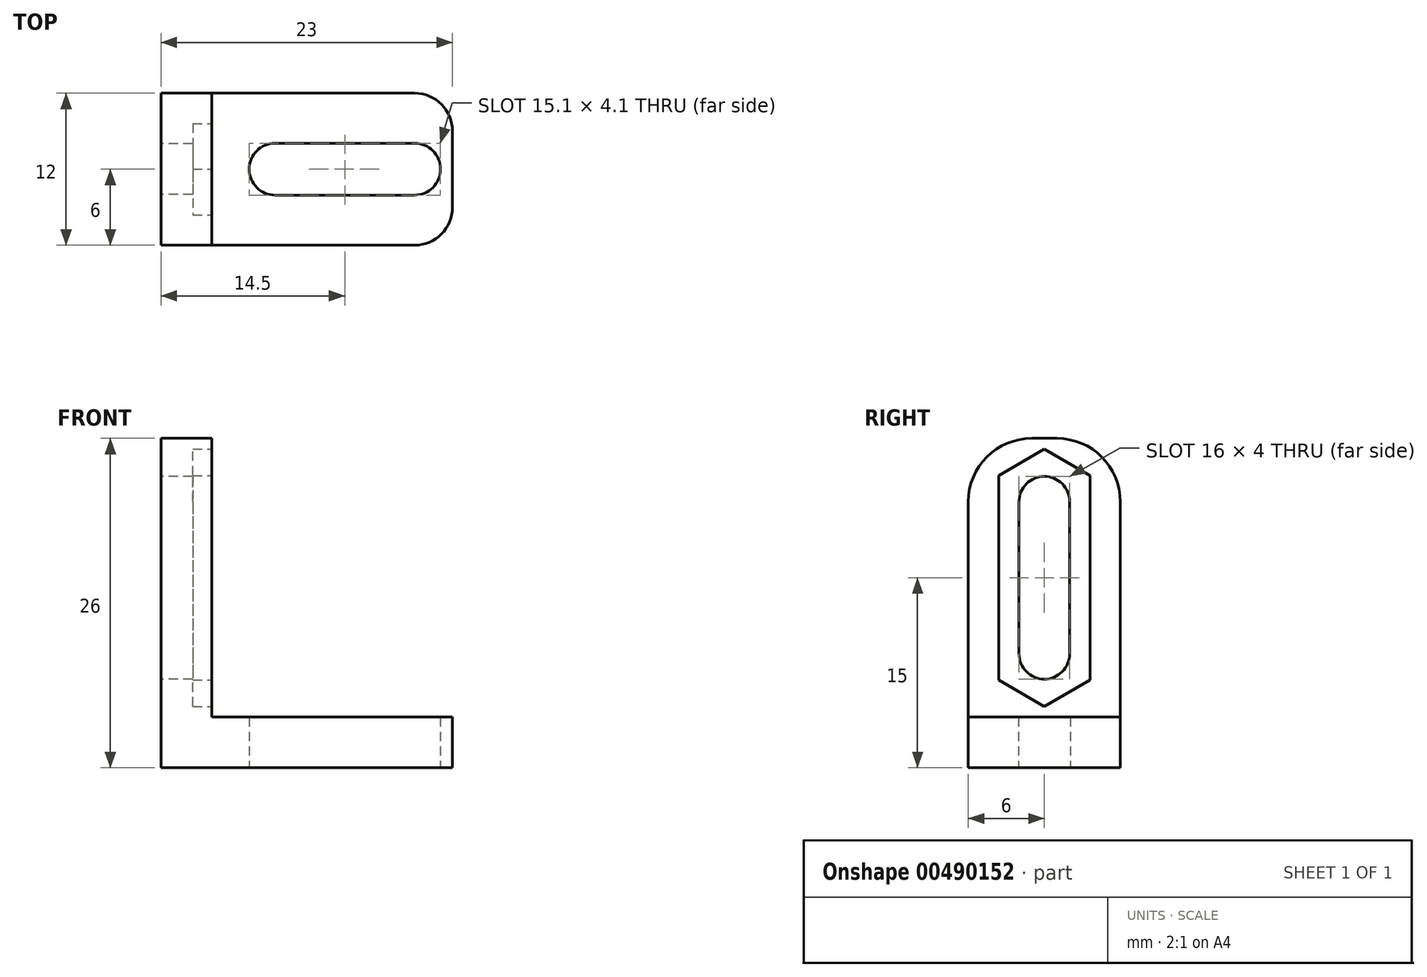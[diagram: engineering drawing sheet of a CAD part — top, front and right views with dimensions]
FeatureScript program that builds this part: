
annotation { "Feature Type Name" : "Feature", "Feature Type Description" : "" }
export const myFeature = defineFeature(function(context is Context, id is Id, definition is map)
    precondition{}
    {
        {
            var Q0;
            Q0=qCreatedBy(makeId("Top.planeOp"),FACE);
            var sketch = newSketch(context, id + "F0", { "sketchPlane" : qUnion([Q0])});
            skLineSegment(sketch, "E0.bottom", {"start": v(-3, 0) * mm, "end": v(-23, 0) * mm});
            skLineSegment(sketch, "E0.top", {"start": v(-3, -12) * mm, "end": v(-23, -12) * mm});
            skLineSegment(sketch, "E0.left", {"start": v(0, -3) * mm, "end": v(0, -9) * mm});
            skLineSegment(sketch, "E0.right", {"start": v(-23, 0) * mm, "end": v(-23, -12) * mm});
            skArc(sketch, "E1", {"start": v(-3, -8.05) * mm, "mid": v(-0.95, -6) * mm, "end": v(-3, -3.95) * mm});
            skPoint(sketch, "E1.centerSnap0", {"position": v(0, -6) * mm});
            skPoint(sketch, "E2.visualSharp", {"position": v(0, 0) * mm});
            skArc(sketch, "E2.filletArc", {"start": v(0, -3) * mm, "mid": v(-0.88, -0.88) * mm, "end": v(-3, 0) * mm});
            skPoint(sketch, "E3.visualSharp", {"position": v(0, -12) * mm});
            skArc(sketch, "E3.filletArc", {"start": v(-3, -12) * mm, "mid": v(-0.88, -11.12) * mm, "end": v(0, -9) * mm});
            skArc(sketch, "E4", {"start": v(-14, -3.95) * mm, "mid": v(-16.05, -6) * mm, "end": v(-14, -8.05) * mm});
            skLineSegment(sketch, "E5", {"start": v(-14, -3.95) * mm, "end": v(-3, -3.95) * mm});
            skLineSegment(sketch, "E6", {"start": v(-14, -8.05) * mm, "end": v(-3, -8.05) * mm});
            skSolve(sketch);
        }
        {
            var Q0;
            Q0=makeQuery(id+"F0.imprint","IMPRINT",FACE,{"disambiguationData":[TD([[makeQuery(id+"F0.imprint","IMPRINT",EDGE,{"derivedFrom":sQuery(id+"F0.wireOp",EDGE,"E0.bottom")}),1.0]])]});
            extrude(context, id + "F1", {"entities" : qUnion([Q0]), "depth" : 4 * mm, "offsetDistance" : 25 * mm});
        }
        {
            var Q0;
            Q0=makeQuery(id+"F1.opExtrude","CAP_FACE",FACE,{"disambiguationData":[OSD([sQuery(id+"F0.wireOp",EDGE,"E0.bottom"),sQuery(id+"F0.wireOp",EDGE,"E0.top"),sQuery(id+"F0.wireOp",EDGE,"E0.left"),sQuery(id+"F0.wireOp",EDGE,"E0.right"),sQuery(id+"F0.wireOp",EDGE,"E1")])],"isStart":false});
            var sketch = newSketch(context, id + "F2", { "sketchPlane" : qUnion([Q0])});
            skLineSegment(sketch, "E7.bottom", {"start": v(-23, 0) * mm, "end": v(-19, 0) * mm});
            skLineSegment(sketch, "E7.top", {"start": v(-23, -12) * mm, "end": v(-19, -12) * mm});
            skLineSegment(sketch, "E7.left", {"start": v(-23, 0) * mm, "end": v(-23, -12) * mm});
            skLineSegment(sketch, "E7.right", {"start": v(-19, 0) * mm, "end": v(-19, -12) * mm});
            skSolve(sketch);
        }
        {
            var Q0;
            Q0=makeQuery(id+"F2.imprint","IMPRINT",FACE,{"disambiguationData":[TD([[makeQuery(id+"F2.imprint","IMPRINT",EDGE,{"derivedFrom":sQuery(id+"F2.wireOp",EDGE,"E7.bottom")}),1.0]])]});
            extrude(context, id + "F3", {"entities" : qUnion([Q0]), "operationType" : NewBodyOperationType.ADD, "depth" : 22 * mm, "offsetDistance" : 25 * mm});
        }
        {
            var Q0;
            Q0=makeQuery(id+"F3.boolean.opBoolean","MERGE",FACE,{"derivedFrom":[makeQuery(id+"F1.opExtrude","SWEPT_FACE",FACE,{"disambiguationData":[OSD([sQuery(id+"F0.wireOp",EDGE,"E0.right")])]}),makeQuery(id+"F3.opExtrude","SWEPT_FACE",FACE,{"disambiguationData":[OSD([sQuery(id+"F2.wireOp",EDGE,"E7.left")])]})]});
            var sketch = newSketch(context, id + "F4", { "sketchPlane" : qUnion([Q0])});
            skLineSegment(sketch, "E8.bottom", {"start": v(6, 7) * mm, "end": v(6, 7) * mm});
            skLineSegment(sketch, "E8.top", {"start": v(6, 23) * mm, "end": v(6, 23) * mm});
            skLineSegment(sketch, "E8.left", {"start": v(4, 9) * mm, "end": v(4, 21) * mm});
            skLineSegment(sketch, "E8.right", {"start": v(8, 9) * mm, "end": v(8, 21) * mm});
            skPoint(sketch, "E8.middle.positionSnap0", {"position": v(6, 26) * mm});
            skPoint(sketch, "E8.middle.positionSnap1", {"position": v(0, 13) * mm});
            skPoint(sketch, "E8.centerSnap0", {"position": v(6, 26) * mm});
            skPoint(sketch, "E8.centerSnap1", {"position": v(0, 13) * mm});
            skPoint(sketch, "E9.endSnap0", {"position": v(6, 23) * mm});
            skPoint(sketch, "E10.visualSharp", {"position": v(4, 23) * mm});
            skArc(sketch, "E10.filletArc", {"start": v(6, 23) * mm, "mid": v(4.59, 22.41) * mm, "end": v(4, 21) * mm});
            skPoint(sketch, "E11.visualSharp", {"position": v(8, 23) * mm});
            skArc(sketch, "E11.filletArc", {"start": v(8, 21) * mm, "mid": v(7.41, 22.41) * mm, "end": v(6, 23) * mm});
            skPoint(sketch, "E12.visualSharp", {"position": v(4, 7) * mm});
            skArc(sketch, "E12.filletArc", {"start": v(4, 9) * mm, "mid": v(4.59, 7.59) * mm, "end": v(6, 7) * mm});
            skPoint(sketch, "E13.visualSharp", {"position": v(8, 7) * mm});
            skArc(sketch, "E13.filletArc", {"start": v(6, 7) * mm, "mid": v(7.41, 7.59) * mm, "end": v(8, 9) * mm});
            skSolve(sketch);
        }
        {
            var Q0;
            {var subQ0=sQuery(id+"F4.wireOp",EDGE,"RQtTgkD9-o44A-vPuf-tJUK-ipy2fORFHTHQ");var subQ1=sQuery(id+"F2.wireOp",EDGE,"E7.left");var subQ4=makeQuery(id+"F3.opExtrude","CAP_EDGE",EDGE,{"disambiguationData":[OSD([subQ1])],"isStart":false});var subQ5=makeQuery(id+"F4.imprint","INTERSECT",VERTEX,{"derivedFrom":[subQ4,subQ0]});Q0=makeQuery(id+"F4.imprint","IMPRINT",FACE,{"disambiguationData":[TD([[makeQuery(id+"F4.imprint","IMPRINT",EDGE,{"disambiguationData":[TD([[subQ5,-1.0]])],"derivedFrom":subQ0}),-1.0]])]});}
            var Q1;
            {var subQ0=sQuery(id+"F4.wireOp",EDGE,"15afa2bb-f388-4f38-a472-24435c0ba0730.MirrorCS");var subQ1=sQuery(id+"F2.wireOp",EDGE,"E7.left");var subQ4=makeQuery(id+"F3.opExtrude","CAP_EDGE",EDGE,{"disambiguationData":[OSD([subQ1])],"isStart":false});var subQ5=makeQuery(id+"F4.imprint","INTERSECT",VERTEX,{"derivedFrom":[subQ4,subQ0]});Q1=makeQuery(id+"F4.imprint","IMPRINT",FACE,{"disambiguationData":[TD([[makeQuery(id+"F4.imprint","IMPRINT",EDGE,{"disambiguationData":[TD([[subQ5,-1.0]])],"derivedFrom":subQ0}),1.0]])]});}
            var Q2;
            Q2=makeQuery(id+"F4.imprint","IMPRINT",FACE,{"disambiguationData":[TD([[makeQuery(id+"F4.imprint","IMPRINT",EDGE,{"derivedFrom":sQuery(id+"F4.wireOp",EDGE,"E8.left")}),-1.0]])]});
            extrude(context, id + "F5", {"entities" : qUnion([Q0, Q1, Q2]), "operationType" : NewBodyOperationType.REMOVE, "oppositeDirection" : true, "depth" : 25 * mm, "offsetDistance" : 25 * mm});
        }
        {
            var Q0;
            Q0=makeQuery(id+"F3.opExtrude","SWEPT_FACE",FACE,{"disambiguationData":[OSD([sQuery(id+"F2.wireOp",EDGE,"E7.right")])]});
            var sketch = newSketch(context, id + "F6", { "sketchPlane" : qUnion([Q0])});
            skPoint(sketch, "E14.middle.positionSnap1", {"position": v(-8, 15) * mm});
            skPoint(sketch, "E14.centerSnap1", {"position": v(-8, 15) * mm});
            skLineSegment(sketch, "E15", {"start": v(-4, 15) * mm, "end": v(-8, 15) * mm, "construction": true});
            skLineSegment(sketch, "E16", {"start": v(-6, 7) * mm, "end": v(-6, 23) * mm, "construction": true});
            skLineSegment(sketch, "E17", {"start": v(-8, 9) * mm, "end": v(-4, 9) * mm, "construction": true});
            skLineSegment(sketch, "E18.1", {"start": v(-2.4, 6.92) * mm, "end": v(-6, 4.84) * mm});
            skLineSegment(sketch, "E18.2", {"start": v(-6, 4.84) * mm, "end": v(-9.6, 6.92) * mm});
            skLineSegment(sketch, "E19.MirrorCS", {"start": v(-6, 25.16) * mm, "end": v(-9.6, 23.08) * mm});
            skLineSegment(sketch, "E20.MirrorCS", {"start": v(-2.4, 23.08) * mm, "end": v(-6, 25.16) * mm});
            skLineSegment(sketch, "E21", {"start": v(-9.6, 23.08) * mm, "end": v(-9.6, 6.92) * mm});
            skLineSegment(sketch, "E22", {"start": v(-2.4, 23.08) * mm, "end": v(-2.4, 6.92) * mm});
            skSolve(sketch);
        }
        {
            var Q0;
            Q0=makeQuery(id+"F6.imprint","IMPRINT",FACE,{"disambiguationData":[TD([[makeQuery(id+"F6.imprint","IMPRINT",EDGE,{"derivedFrom":sQuery(id+"F6.wireOp",EDGE,"E18.1")}),-1.0]])]});
            extrude(context, id + "F7", {"entities" : qUnion([Q0]), "operationType" : NewBodyOperationType.REMOVE, "oppositeDirection" : true, "depth" : 1.5 * mm, "offsetDistance" : 25 * mm});
        }
        {
            var Q0;
            Q0=makeQuery(id+"F3.opExtrude","CAP_EDGE",EDGE,{"disambiguationData":[OSD([sQuery(id+"F2.wireOp",EDGE,"E7.top")])],"isStart":false});
            var Q1;
            Q1=makeQuery(id+"F3.opExtrude","CAP_EDGE",EDGE,{"disambiguationData":[OSD([sQuery(id+"F2.wireOp",EDGE,"E7.bottom")])],"isStart":false});
            fillet(context, id + "F8", {"entities" : qUnion([Q0, Q1]), "radius" : 5 * mm, "tangentPropagation" : true, "allowEdgeOverflow" : false});
        }
    });
